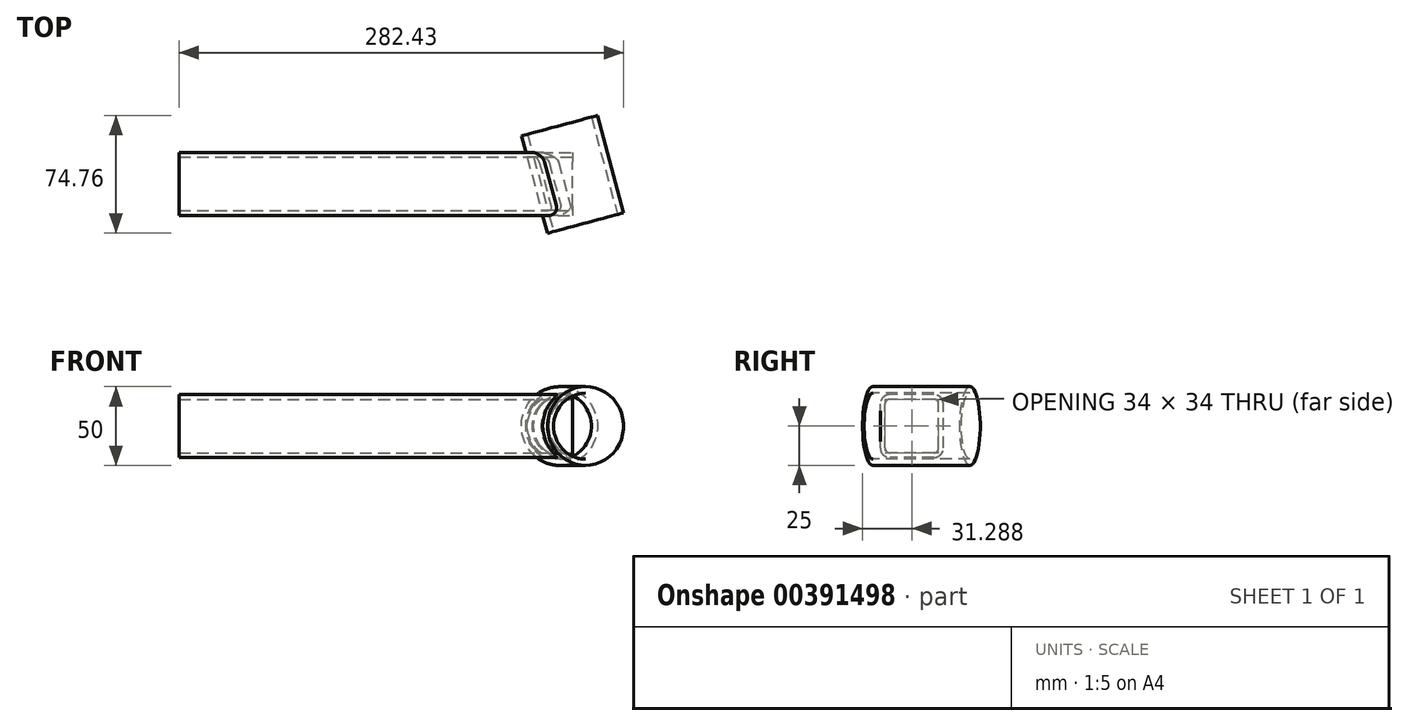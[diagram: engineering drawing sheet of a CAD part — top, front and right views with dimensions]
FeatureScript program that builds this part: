
annotation { "Feature Type Name" : "Feature", "Feature Type Description" : "" }
export const myFeature = defineFeature(function(context is Context, id is Id, definition is map)
    precondition{}
    {
        {
            var Q0;
            Q0=qCreatedBy(makeId("Front.planeOp"),FACE);
            var sketch = newSketch(context, id + "F0", { "sketchPlane" : qUnion([Q0])});
            skCircle(sketch, "E0", {"center": v(0, 0) * mm, "radius": 21 * mm});
            skCircle(sketch, "E1.0", {"center": v(0, 0) * mm, "radius": 25 * mm});
            skLineSegment(sketch, "E2", {"start": v(0, 0) * mm, "end": v(0, -58.25) * mm, "construction": true});
            skLineSegment(sketch, "E3", {"start": v(-25, 0) * mm, "end": v(-25, 46.06) * mm, "construction": true});
            skPoint(sketch, "E4", {"position": v(-25, 0) * mm});
            skSolve(sketch);
        }
        {
            var Q0;
            Q0=makeQuery(id+"F0.imprint","IMPRINT",FACE,{"disambiguationData":[TD([[makeQuery(id+"F0.imprint","IMPRINT",EDGE,{"derivedFrom":sQuery(id+"F0.wireOp",EDGE,"E0")}),-1.0]])]});
            extrude(context, id + "F1", {"entities" : qUnion([Q0]), "depth" : 64 * mm, "symmetric" : true});
        }
        {
            var Q0;
            Q0=makeQuery(id+"F1.opExtrude","SWEPT_BODY",BODY,{"disambiguationData":[OSD([sQuery(id+"F0.wireOp",EDGE,"E0"),sQuery(id+"F0.wireOp",EDGE,"E1.0")])]});
            var Q1;
            Q1=sQuery(id+"F0.wireOp",EDGE,"E2");
            transform(context, id + "F2", {"entities" : qUnion([Q0]), "transformType" : TransformType.ROTATION, "transformAxis" : qUnion([Q1]), "angle" : 165 * degree, "makeCopy" : false});
        }
        {
            var Q0;
            Q0=qCreatedBy(makeId("Right.planeOp"),FACE);
            var sketch = newSketch(context, id + "F3", { "sketchPlane" : qUnion([Q0])});
            skLineSegment(sketch, "E5.bottom", {"start": v(-20.1, -20) * mm, "end": v(7.9, -20) * mm});
            skLineSegment(sketch, "E5.top", {"start": v(-20.1, 20) * mm, "end": v(7.9, 20) * mm});
            skLineSegment(sketch, "E5.left", {"start": v(-26.1, -14) * mm, "end": v(-26.1, 14) * mm});
            skLineSegment(sketch, "E5.right", {"start": v(13.9, -14) * mm, "end": v(13.9, 14) * mm});
            skPoint(sketch, "E5.middle", {"position": v(-6.1, 0) * mm});
            skPoint(sketch, "E6.visualSharp", {"position": v(13.9, 20) * mm});
            skArc(sketch, "E6.filletArc", {"start": v(13.9, 14) * mm, "mid": v(12.15, 18.24) * mm, "end": v(7.9, 20) * mm});
            skPoint(sketch, "E7.visualSharp", {"position": v(-26.1, 20) * mm});
            skArc(sketch, "E7.filletArc", {"start": v(-20.1, 20) * mm, "mid": v(-24.33, 18.24) * mm, "end": v(-26.1, 14) * mm});
            skPoint(sketch, "E8.visualSharp", {"position": v(13.9, -20) * mm});
            skArc(sketch, "E8.filletArc", {"start": v(7.9, -20) * mm, "mid": v(12.15, -18.24) * mm, "end": v(13.9, -14) * mm});
            skPoint(sketch, "E9.visualSharp", {"position": v(-26.1, -20) * mm});
            skArc(sketch, "E9.filletArc", {"start": v(-26.1, -14) * mm, "mid": v(-24.33, -18.24) * mm, "end": v(-20.1, -20) * mm});
            skLineSegment(sketch, "E10.bottom", {"start": v(-20.1, -17) * mm, "end": v(7.9, -17) * mm});
            skLineSegment(sketch, "E10.top", {"start": v(-20.1, 17) * mm, "end": v(7.9, 17) * mm});
            skLineSegment(sketch, "E10.left", {"start": v(-23.1, -14) * mm, "end": v(-23.1, 14) * mm});
            skLineSegment(sketch, "E10.right", {"start": v(10.9, -14) * mm, "end": v(10.9, 14) * mm});
            skPoint(sketch, "E11.visualSharp", {"position": v(-23.1, 17) * mm});
            skArc(sketch, "E11.filletArc", {"start": v(-20.1, 17) * mm, "mid": v(-22.21, 16.12) * mm, "end": v(-23.1, 14) * mm});
            skPoint(sketch, "E12.visualSharp", {"position": v(-23.1, -17) * mm});
            skArc(sketch, "E12.filletArc", {"start": v(-23.1, -14) * mm, "mid": v(-22.21, -16.12) * mm, "end": v(-20.1, -17) * mm});
            skPoint(sketch, "E13.visualSharp", {"position": v(10.9, -17) * mm});
            skArc(sketch, "E13.filletArc", {"start": v(7.9, -17) * mm, "mid": v(10.03, -16.12) * mm, "end": v(10.9, -14) * mm});
            skPoint(sketch, "E14.visualSharp", {"position": v(10.9, 17) * mm});
            skArc(sketch, "E14.filletArc", {"start": v(10.9, 14) * mm, "mid": v(10.03, 16.12) * mm, "end": v(7.9, 17) * mm});
            skSolve(sketch);
        }
        {
            var Q0;
            Q0=makeQuery(id+"F3.imprint","IMPRINT",FACE,{"disambiguationData":[TD([[makeQuery(id+"F3.imprint","IMPRINT",EDGE,{"derivedFrom":sQuery(id+"F3.wireOp",EDGE,"E5.bottom")}),1.0]])]});
            extrude(context, id + "F4", {"entities" : qUnion([Q0]), "operationType" : NewBodyOperationType.ADD, "oppositeDirection" : true, "depth" : 250 * mm});
        }
    });
